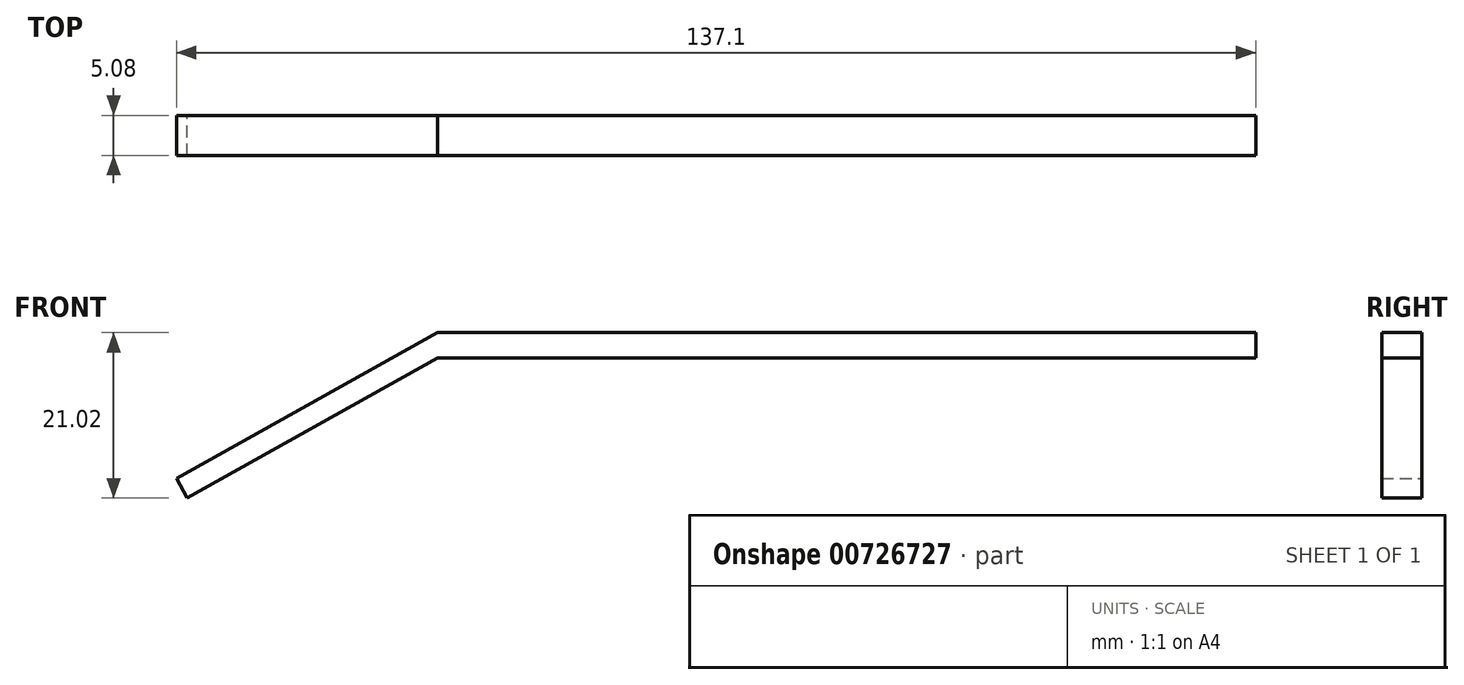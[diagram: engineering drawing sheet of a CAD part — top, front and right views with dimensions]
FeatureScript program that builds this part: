
annotation { "Feature Type Name" : "Feature", "Feature Type Description" : "" }
export const myFeature = defineFeature(function(context is Context, id is Id, definition is map)
    precondition{}
    {
        {
            var Q0;
            Q0=qCreatedBy(makeId("Front.planeOp"),FACE);
            var sketch = newSketch(context, id + "F0", { "sketchPlane" : qUnion([Q0])});
            skLineSegment(sketch, "E0", {"start": v(49.25, 10.43) * mm, "end": v(-41.13, 10.43) * mm});
            skLineSegment(sketch, "E1", {"start": v(-41.13, 10.43) * mm, "end": v(-69.95, 27.45) * mm});
            skLineSegment(sketch, "E2", {"start": v(-69.95, 27.45) * mm, "end": v(-71.83, 24.26) * mm});
            skLineSegment(sketch, "E3", {"start": v(-71.83, 24.26) * mm, "end": v(-42.7, 7.06) * mm});
            skLineSegment(sketch, "E4", {"start": v(-42.7, 7.06) * mm, "end": v(49.25, 7.06) * mm});
            skLineSegment(sketch, "E5", {"start": v(49.25, 10.43) * mm, "end": v(49.25, 7.06) * mm});
            skSolve(sketch);
        }
        {
            var Q0;
            Q0 = qSketchRegion(id + "F0", true);
            extrude(context, id + "F1", {"entities" : qUnion([Q0]), "depth" : 5.08 * mm, "offsetDistance" : 25.4 * mm});
        }
        {
            var Q0;
            Q0=makeQuery(id+"F1.opExtrude","SWEPT_BODY",BODY,{"disambiguationData":[OSD([sQuery(id+"F0.wireOp",EDGE,"E0"),sQuery(id+"F0.wireOp",EDGE,"E1"),sQuery(id+"F0.wireOp",EDGE,"E2"),sQuery(id+"F0.wireOp",EDGE,"E3"),sQuery(id+"F0.wireOp",EDGE,"E4"),sQuery(id+"F0.wireOp",EDGE,"E5")])]});
            deleteBodies(context, id + "F2", {"entities" : qUnion([Q0])});
        }
        {
            var Q0;
            Q0=qCreatedBy(makeId("Front.planeOp"),FACE);
            var sketch = newSketch(context, id + "F3", { "sketchPlane" : qUnion([Q0])});
            skLineSegment(sketch, "E6", {"start": v(64.41, 8.53) * mm, "end": v(-31.2, 8.53) * mm});
            skLineSegment(sketch, "E7", {"start": v(-31.2, 8.53) * mm, "end": v(-64.64, -7.4) * mm});
            skLineSegment(sketch, "E8", {"start": v(-64.64, -7.4) * mm, "end": v(-66.74, -2.99) * mm});
            skLineSegment(sketch, "E9", {"start": v(-66.74, -2.99) * mm, "end": v(-31.2, 13.95) * mm});
            skLineSegment(sketch, "E10", {"start": v(-31.2, 13.95) * mm, "end": v(63.51, 13.95) * mm});
            skLineSegment(sketch, "E11", {"start": v(63.51, 13.95) * mm, "end": v(64.41, 8.53) * mm});
            skSolve(sketch);
        }
        {
            var Q0;
            Q0 = qSketchRegion(id + "F3", true);
            extrude(context, id + "F4", {"entities" : qUnion([Q0]), "depth" : 5.08 * mm, "offsetDistance" : 25.4 * mm});
        }
        {
            var Q0;
            Q0=makeQuery(id+"F4.opExtrude","SWEPT_BODY",BODY,{"disambiguationData":[OSD([sQuery(id+"F3.wireOp",EDGE,"E6"),sQuery(id+"F3.wireOp",EDGE,"E7"),sQuery(id+"F3.wireOp",EDGE,"E8"),sQuery(id+"F3.wireOp",EDGE,"E9"),sQuery(id+"F3.wireOp",EDGE,"E10"),sQuery(id+"F3.wireOp",EDGE,"E11")])]});
            deleteBodies(context, id + "F5", {"entities" : qUnion([Q0])});
        }
        {
            var Q0;
            Q0=qCreatedBy(makeId("Front.planeOp"),FACE);
            var sketch = newSketch(context, id + "F6", { "sketchPlane" : qUnion([Q0])});
            skLineSegment(sketch, "E12", {"start": v(61.67, 10.92) * mm, "end": v(-42.24, 10.92) * mm});
            skLineSegment(sketch, "E13", {"start": v(-42.24, 10.92) * mm, "end": v(-75.43, -7.64) * mm});
            skLineSegment(sketch, "E14", {"start": v(-75.43, -7.64) * mm, "end": v(-74.05, -10.1) * mm});
            skLineSegment(sketch, "E15", {"start": v(-74.05, -10.1) * mm, "end": v(-42.24, 7.69) * mm});
            skLineSegment(sketch, "E16", {"start": v(-42.24, 7.69) * mm, "end": v(61.67, 7.69) * mm});
            skLineSegment(sketch, "E17", {"start": v(61.67, 7.69) * mm, "end": v(61.67, 10.92) * mm});
            skSolve(sketch);
        }
        {
            var Q0;
            Q0 = qSketchRegion(id + "F6", true);
            extrude(context, id + "F7", {"entities" : qUnion([Q0]), "depth" : 5.08 * mm, "offsetDistance" : 25.4 * mm});
        }
    });
